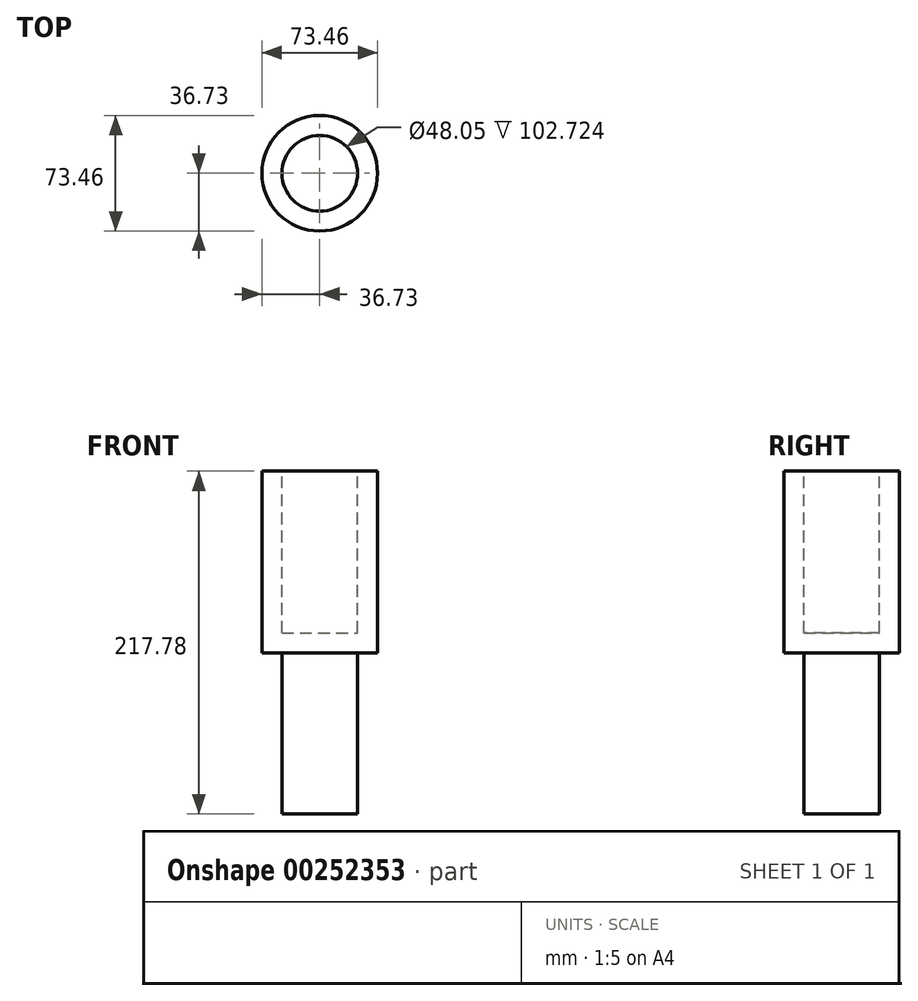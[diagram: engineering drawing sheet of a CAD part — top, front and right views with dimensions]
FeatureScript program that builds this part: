
annotation { "Feature Type Name" : "Feature", "Feature Type Description" : "" }
export const myFeature = defineFeature(function(context is Context, id is Id, definition is map)
    precondition{}
    {
        {
            var Q0;
            Q0=qCreatedBy(makeId("Front.planeOp"),FACE);
            var sketch = newSketch(context, id + "F0", { "sketchPlane" : qUnion([Q0])});
            skLineSegment(sketch, "E0.bottom", {"start": v(-36.73, 53.2) * mm, "end": v(36.73, 53.2) * mm});
            skLineSegment(sketch, "E0.top", {"start": v(-36.73, -62.23) * mm, "end": v(36.73, -62.23) * mm});
            skLineSegment(sketch, "E0.left", {"start": v(-36.73, 53.2) * mm, "end": v(-36.73, -62.23) * mm});
            skLineSegment(sketch, "E0.right", {"start": v(36.73, 53.2) * mm, "end": v(36.73, -62.23) * mm});
            skPoint(sketch, "E0.middle", {"position": v(0, -4.52) * mm});
            skLineSegment(sketch, "E1", {"start": v(0, 53.2) * mm, "end": v(0, -62.23) * mm});
            skSolve(sketch);
        }
        {
            var Q0;
            {var subQ0=sQuery(id+"F0.wireOp",EDGE,"E0.left");Q0=makeQuery(id+"F0.imprint","IMPRINT",FACE,{"disambiguationData":[TD([[makeQuery(id+"F0.imprint","IMPRINT",EDGE,{"derivedFrom":subQ0}),1.0]])]});}
            var Q1;
            Q1=sQuery(id+"F0.wireOp",EDGE,"E1");
            revolve(context, id + "F1", {"entities" : qUnion([Q0]), "axis" : qUnion([Q1]), "revolveType" : RevolveType.FULL});
        }
        {
            var Q0;
            Q0=makeQuery(id+"F1.opRevolve","SWEPT_FACE",FACE,{"disambiguationData":[OSD([sQuery(id+"F0.wireOp",EDGE,"E0.bottom")])]});
            shell(context, id + "F2", {"entities" : qUnion([Q0]), "thickness" : 12.7 * mm});
        }
        {
            var Q0;
            Q0=makeQuery(id+"F2.opShell","OFFSET_FACE",FACE,{"disambiguationData":[OSD([sQuery(id+"F0.wireOp",EDGE,"E0.top")])]});
            extrude(context, id + "F3", {"entities" : qUnion([Q0]), "operationType" : NewBodyOperationType.ADD, "oppositeDirection" : true, "depth" : 115.06 * mm});
        }
    });
